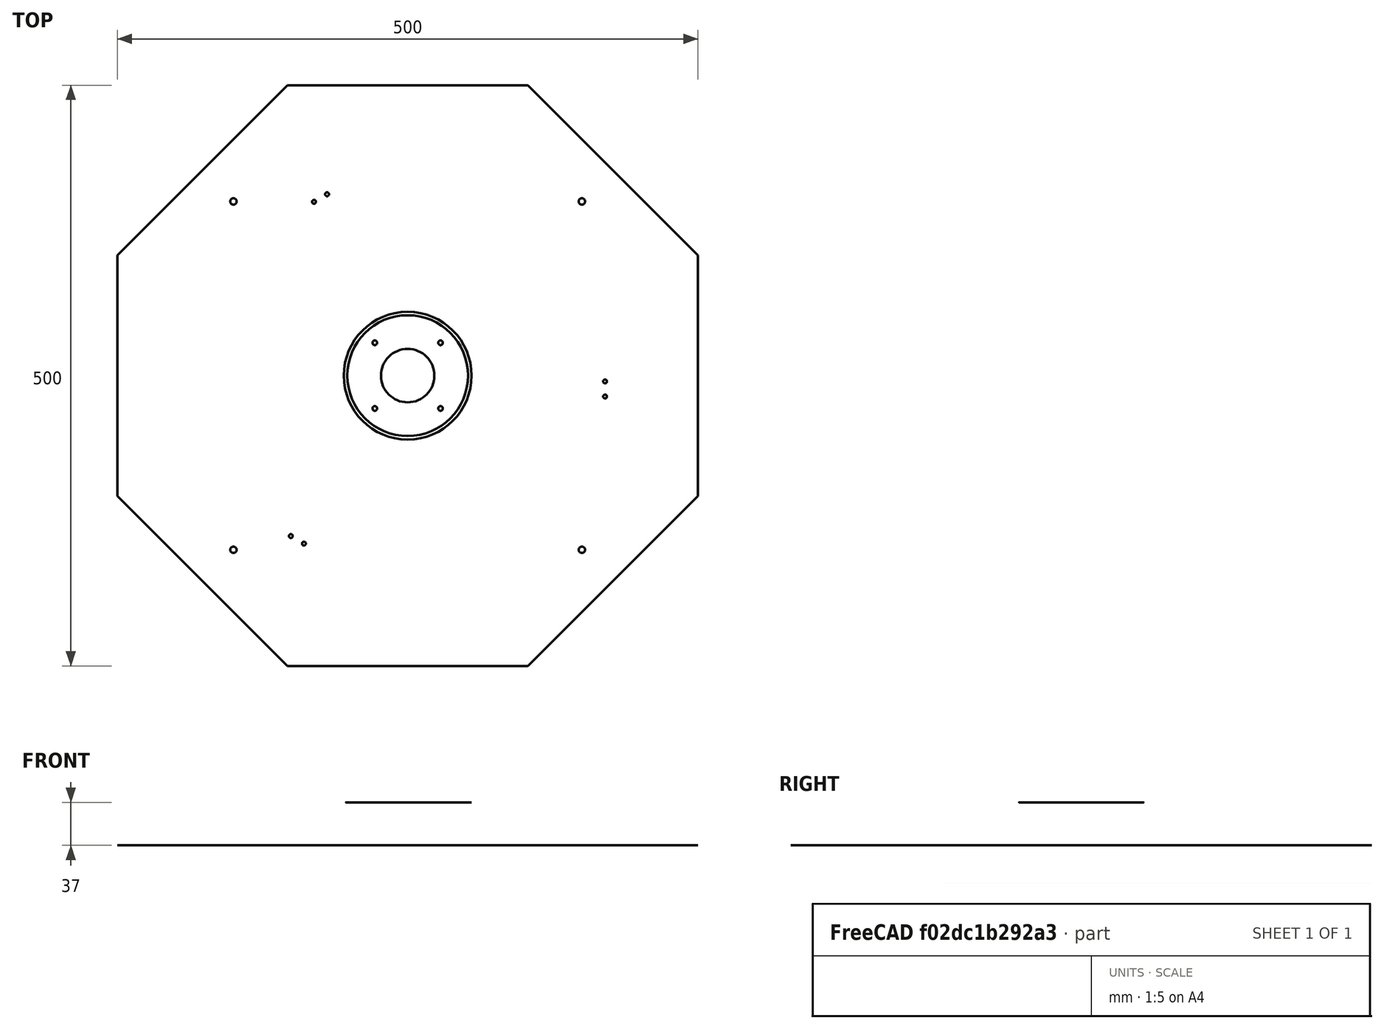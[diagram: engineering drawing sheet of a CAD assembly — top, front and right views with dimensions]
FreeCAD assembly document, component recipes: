
FREECAD ASSEMBLY — COMPONENT RECIPES ("Baugruppe_Lampe_4er")

This assembly document has 10 components, labeled P0..P9 below (a component is one placed body or linked part). 0 of them carry a construction recipe — the FreeCAD feature program that regenerates the part from scratch, quoted from this document or its linked companion documents; the rest are supplied as boundary geometry only. No exploded tour is included for this assembly.
COMPONENT P0 — geometry summary ("Body"; no construction recipe available for this part):
  bounding box: 500.0 x 500.0 x 1.0 mm
  tessellated surface: 9,928 triangles
  volume: 203447 mm^3 (81% of its bounding box)
  symmetry: 2-fold rotationally symmetric about the x axis; 2-fold rotationally symmetric about the y axis; 4-fold rotationally symmetric about the z axis; mirror-symmetric across its x mid-plane, y mid-plane, z mid-plane
COMPONENT P1 — geometry summary ("Body001"; no construction recipe available for this part):
  bounding box: 127.2 x 110.0 x 67.0 mm
  tessellated surface: 5,338 triangles
  volume: 220714 mm^3 (24% of its bounding box)
  symmetry: 2-fold rotationally symmetric about the z axis; mirror-symmetric across its x mid-plane, y mid-plane
COMPONENT P2 — geometry summary ("Body002"; no construction recipe available for this part):
  bounding box: 137.3 x 83.2 x 71.4 mm
  tessellated surface: 10,066 triangles
  volume: 209287 mm^3 (26% of its bounding box)
COMPONENT P3 — geometry summary ("Body003"; no construction recipe available for this part):
  bounding box: 137.3 x 83.2 x 71.4 mm
  tessellated surface: 10,066 triangles
  volume: 209287 mm^3 (26% of its bounding box)
COMPONENT P4 — geometry summary ("Body004"; no construction recipe available for this part):
  bounding box: 137.3 x 83.2 x 71.4 mm
  tessellated surface: 10,066 triangles
  volume: 209287 mm^3 (26% of its bounding box)
COMPONENT P5 — geometry summary ("Wago_5x_flach"; no construction recipe available for this part):
  bounding box: 54.2 x 21.2 x 11.0 mm
  tessellated surface: 2,646 triangles
  volume: 2738 mm^3 (22% of its bounding box)
  symmetry: mirror-symmetric across its y mid-plane
COMPONENT P6 — geometry summary ("Wago_5x_flach001"; no construction recipe available for this part):
  bounding box: 54.2 x 21.2 x 11.0 mm
  tessellated surface: 2,646 triangles
  volume: 2738 mm^3 (22% of its bounding box)
  symmetry: mirror-symmetric across its y mid-plane
COMPONENT P7 — geometry summary ("Body005"; no construction recipe available for this part):
  bounding box: 137.3 x 83.2 x 71.4 mm
  tessellated surface: 10,066 triangles
  volume: 209287 mm^3 (26% of its bounding box)
COMPONENT P8 — geometry summary ("Wago_5x_flach002"; no construction recipe available for this part):
  bounding box: 54.2 x 21.2 x 11.0 mm
  tessellated surface: 2,646 triangles
  volume: 2738 mm^3 (22% of its bounding box)
  symmetry: mirror-symmetric across its y mid-plane
COMPONENT P9 — geometry summary ("Wago_5x_flach003"; no construction recipe available for this part):
  bounding box: 54.2 x 21.2 x 11.0 mm
  tessellated surface: 2,646 triangles
  volume: 2738 mm^3 (22% of its bounding box)
  symmetry: mirror-symmetric across its y mid-plane
PROVENANCE & LICENSES
A FreeCAD (.FCStd) document from a public repository crawl; recipes are the document's own serialized feature recipes (and, for linked parts, companion documents' recipes).
License: as declared in the source repository (recorded in the dataset sidecar).
